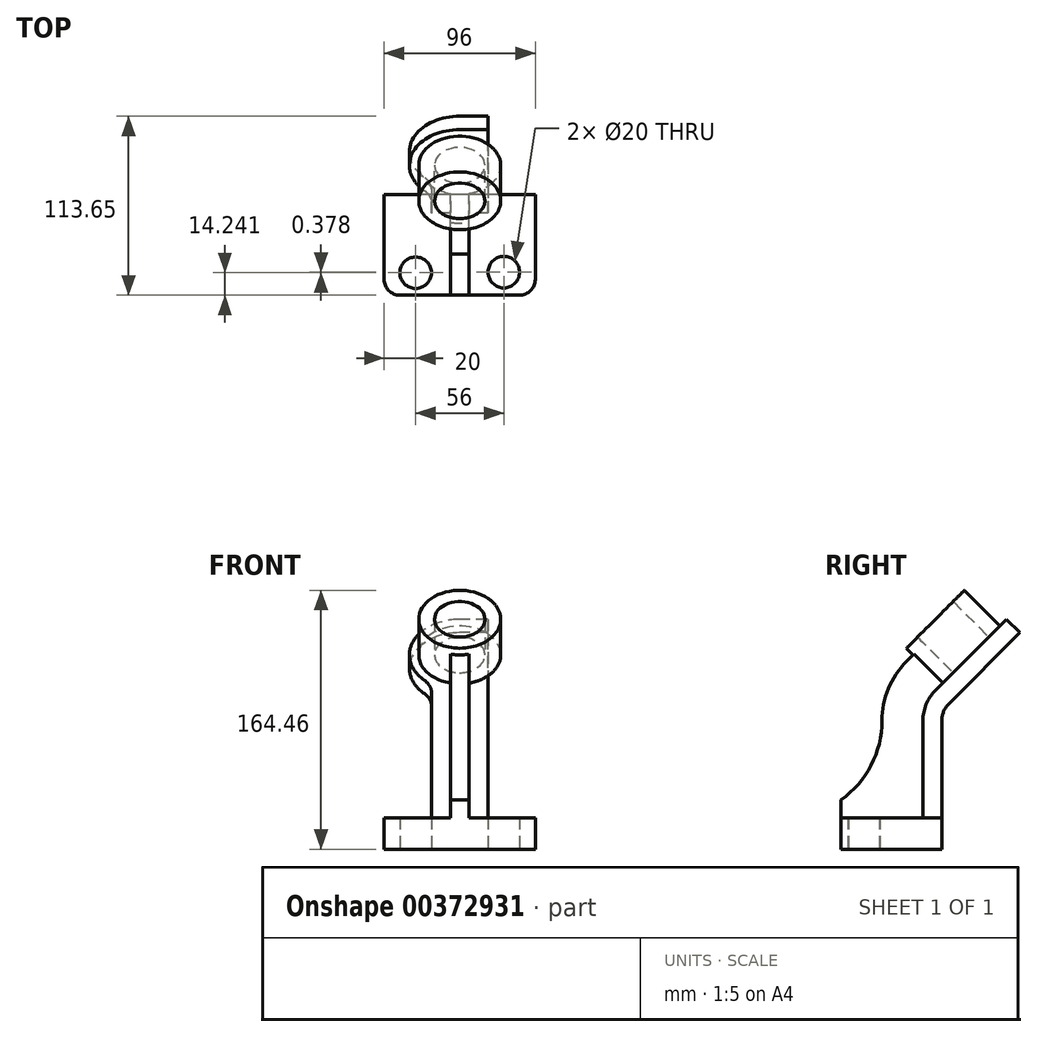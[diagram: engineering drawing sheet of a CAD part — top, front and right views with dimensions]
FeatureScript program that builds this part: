
annotation { "Feature Type Name" : "Feature", "Feature Type Description" : "" }
export const myFeature = defineFeature(function(context is Context, id is Id, definition is map)
    precondition{}
    {
        {
            var Q0;
            Q0=qCreatedBy(makeId("Top.planeOp"),FACE);
            var sketch = newSketch(context, id + "F0", { "sketchPlane" : qUnion([Q0])});
            skLineSegment(sketch, "E0.bottom", {"start": v(48, -32) * mm, "end": v(-48, -32) * mm});
            skLineSegment(sketch, "E0.top", {"start": v(48, 32) * mm, "end": v(-48, 32) * mm});
            skLineSegment(sketch, "E0.left", {"start": v(48, -32) * mm, "end": v(48, 32) * mm});
            skLineSegment(sketch, "E0.right", {"start": v(-48, -32) * mm, "end": v(-48, 32) * mm});
            skPoint(sketch, "E0.middle", {"position": v(0, 0) * mm});
            skCircle(sketch, "E1", {"center": v(28, -17.38) * mm, "radius": 10 * mm});
            skCircle(sketch, "E2", {"center": v(-28, -17.76) * mm, "radius": 10 * mm});
            skSolve(sketch);
        }
        {
            var Q0;
            Q0=makeQuery(id+"F0.imprint","IMPRINT",FACE,{"disambiguationData":[TD([[makeQuery(id+"F0.imprint","IMPRINT",EDGE,{"derivedFrom":sQuery(id+"F0.wireOp",EDGE,"E0.bottom")}),-1.0]])]});
            extrude(context, id + "F1", {"entities" : qUnion([Q0]), "depth" : 20 * mm});
        }
        {
            var Q0;
            Q0=makeQuery(id+"F1.opExtrude","SWEPT_EDGE",EDGE,{"disambiguationData":[OSD([sQuery(id+"F0.wireOp",EDGE,"E0.bottom"),sQuery(id+"F0.wireOp",EDGE,"E0.left")])]});
            var Q1;
            Q1=makeQuery(id+"F1.opExtrude","SWEPT_EDGE",EDGE,{"disambiguationData":[OSD([sQuery(id+"F0.wireOp",EDGE,"E0.bottom"),sQuery(id+"F0.wireOp",EDGE,"E0.right")])]});
            fillet(context, id + "F2", {"entities" : qUnion([Q0, Q1]), "radius" : 10 * mm, "tangentPropagation" : true, "allowEdgeOverflow" : false});
        }
        {
            var Q0;
            Q0=qCreatedBy(makeId("Right.planeOp"),FACE);
            var sketch = newSketch(context, id + "F3", { "sketchPlane" : qUnion([Q0])});
            skLineSegment(sketch, "E3", {"start": v(32, 0) * mm, "end": v(32, 81.73) * mm});
            skLineSegment(sketch, "E4", {"start": v(36.4, 92.34) * mm, "end": v(81.65, 137.6) * mm});
            skPoint(sketch, "E5.visualSharp", {"position": v(32, 87.95) * mm});
            skArc(sketch, "E5.filletArc", {"start": v(36.4, 92.34) * mm, "mid": v(33.14, 87.47) * mm, "end": v(32, 81.73) * mm});
            skLineSegment(sketch, "E6", {"start": v(81.65, 137.6) * mm, "end": v(73.16, 146.08) * mm});
            skLineSegment(sketch, "E7", {"start": v(73.16, 146.08) * mm, "end": v(27.9, 100.82) * mm});
            skLineSegment(sketch, "E8", {"start": v(20, 81.73) * mm, "end": v(20, 0) * mm});
            skLineSegment(sketch, "E9", {"start": v(20, 0) * mm, "end": v(32, 0) * mm});
            skPoint(sketch, "E10.visualSharp", {"position": v(20, 92.92) * mm});
            skArc(sketch, "E10.filletArc", {"start": v(27.9, 100.82) * mm, "mid": v(22.06, 92.06) * mm, "end": v(20, 81.73) * mm});
            skSolve(sketch);
        }
        {
            var Q0;
            Q0=makeQuery(id+"F3.imprint","IMPRINT",FACE,{"disambiguationData":[TD([[makeQuery(id+"F3.imprint","IMPRINT",EDGE,{"derivedFrom":sQuery(id+"F3.wireOp",EDGE,"E3")}),1.0]])]});
            extrude(context, id + "F4", {"entities" : qUnion([Q0]), "operationType" : NewBodyOperationType.ADD, "endBound" : BoundingType.SYMMETRIC, "depth" : 36 * mm});
        }
        {
            var Q0;
            Q0=makeQuery(id+"F4.opExtrude","SWEPT_FACE",FACE,{"disambiguationData":[OSD([sQuery(id+"F3.wireOp",EDGE,"E7")])]});
            var sketch = newSketch(context, id + "F5", { "sketchPlane" : qUnion([Q0])});
            skCircle(sketch, "E11", {"center": v(0, 123.03) * mm, "radius": 32 * mm});
            skSolve(sketch);
        }
        {
            var Q0;
            {var subQ0=sQuery(id+"F5.wireOp",EDGE,"E11");var subQ1=makeQuery(id+"F4.opExtrude","CAP_EDGE",EDGE,{"disambiguationData":[OSD([sQuery(id+"F3.wireOp",EDGE,"E7")])],"isStart":true});var subQ2=makeQuery(id+"F5.imprint","INTERSECT",VERTEX,{"disambiguationData":[OD(0.0)],"derivedFrom":[subQ1,subQ0]});Q0=makeQuery(id+"F5.imprint","IMPRINT",FACE,{"disambiguationData":[TD([[makeQuery(id+"F5.imprint","IMPRINT",EDGE,{"disambiguationData":[TD([[subQ2,-1.0]])],"derivedFrom":subQ0}),1.0]])]});}
            var Q1;
            {var subQ0=sQuery(id+"F5.wireOp",EDGE,"E11");var subQ1=sQuery(id+"F3.wireOp",EDGE,"E7");var subQ6=makeQuery(id+"F4.opExtrude","CAP_EDGE",EDGE,{"disambiguationData":[OSD([subQ1])],"isStart":true});var subQ9=makeQuery(id+"F5.imprint","INTERSECT",VERTEX,{"disambiguationData":[OD(0.0)],"derivedFrom":[subQ6,subQ0]});Q1=makeQuery(id+"F5.imprint","IMPRINT",FACE,{"disambiguationData":[TD([[makeQuery(id+"F5.imprint","IMPRINT",EDGE,{"disambiguationData":[TD([[subQ9,-1.0]])],"derivedFrom":subQ6}),1.0]])]});}
            var Q2;
            {var subQ0=sQuery(id+"F5.wireOp",EDGE,"E11");var subQ1=makeQuery(id+"F4.opExtrude","CAP_EDGE",EDGE,{"disambiguationData":[OSD([sQuery(id+"F3.wireOp",EDGE,"E7")])],"isStart":false});var subQ2=makeQuery(id+"F5.imprint","INTERSECT",VERTEX,{"disambiguationData":[OD(0.0)],"derivedFrom":[subQ1,subQ0]});Q2=makeQuery(id+"F5.imprint","IMPRINT",FACE,{"disambiguationData":[TD([[makeQuery(id+"F5.imprint","IMPRINT",EDGE,{"disambiguationData":[TD([[subQ2,1.0]])],"derivedFrom":subQ0}),1.0]])]});}
            extrude(context, id + "F6", {"entities" : qUnion([Q0, Q1, Q2]), "operationType" : NewBodyOperationType.ADD, "oppositeDirection" : true, "depth" : 12 * mm});
        }
        {
            var Q0;
            {var subQ0=sQuery(id+"F5.wireOp",EDGE,"E11");var subQ1=sQuery(id+"F3.wireOp",EDGE,"E7");var subQ4=makeQuery(id+"F4.opExtrude","CAP_EDGE",EDGE,{"disambiguationData":[OSD([subQ1])],"isStart":true});var subQ5=makeQuery(id+"F5.imprint","INTERSECT",VERTEX,{"disambiguationData":[OD(0.0)],"derivedFrom":[subQ4,subQ0]});Q0=makeQuery(id+"F5.imprint","IMPRINT",FACE,{"disambiguationData":[TD([[makeQuery(id+"F5.imprint","IMPRINT",EDGE,{"disambiguationData":[TD([[subQ5,1.0]])],"derivedFrom":subQ0}),-1.0]])]});}
            var Q1;
            {var subQ0=sQuery(id+"F5.wireOp",EDGE,"E11");var subQ1=sQuery(id+"F3.wireOp",EDGE,"E7");var subQ4=makeQuery(id+"F4.opExtrude","CAP_EDGE",EDGE,{"disambiguationData":[OSD([subQ1])],"isStart":false});var subQ5=makeQuery(id+"F5.imprint","INTERSECT",VERTEX,{"disambiguationData":[OD(0.0)],"derivedFrom":[subQ4,subQ0]});Q1=makeQuery(id+"F5.imprint","IMPRINT",FACE,{"disambiguationData":[TD([[makeQuery(id+"F5.imprint","IMPRINT",EDGE,{"disambiguationData":[TD([[subQ5,-1.0]])],"derivedFrom":subQ0}),-1.0]])]});}
            extrude(context, id + "F7", {"entities" : qUnion([Q0, Q1]), "operationType" : NewBodyOperationType.REMOVE, "oppositeDirection" : true, "depth" : 25 * mm});
        }
        {
            var Q0;
            {var subQ0=sQuery(id+"F5.wireOp",EDGE,"E11");var subQ1=sQuery(id+"F3.wireOp",EDGE,"E7");var subQ6=makeQuery(id+"F4.opExtrude","CAP_EDGE",EDGE,{"disambiguationData":[OSD([subQ1])],"isStart":true});var subQ9=makeQuery(id+"F5.imprint","INTERSECT",VERTEX,{"disambiguationData":[OD(0.0)],"derivedFrom":[subQ6,subQ0]});Q0=makeQuery(id+"F5.imprint","IMPRINT",FACE,{"disambiguationData":[TD([[makeQuery(id+"F5.imprint","IMPRINT",EDGE,{"disambiguationData":[TD([[subQ9,-1.0]])],"derivedFrom":subQ6}),1.0]])]});}
            var sketch = newSketch(context, id + "F8", { "sketchPlane" : qUnion([Q0])});
            skCircle(sketch, "E12", {"center": v(0, 123.03) * mm, "radius": 26 * mm});
            skCircle(sketch, "E13", {"center": v(0, 123.03) * mm, "radius": 16 * mm});
            skSolve(sketch);
        }
        {
            var Q0;
            Q0 = qSketchRegion(id + "F8", true);
            extrude(context, id + "F9", {"entities" : qUnion([Q0]), "operationType" : NewBodyOperationType.ADD, "depth" : 32 * mm});
        }
        {
            var Q0;
            Q0=makeQuery(id+"F6.boolean.opBoolean","INTERSECT",EDGE,{"disambiguationData":[OD(0.0)],"derivedFrom":[makeQuery(id+"F4.opExtrude","CAP_FACE",FACE,{"disambiguationData":[OSD([sQuery(id+"F3.wireOp",EDGE,"E3"),sQuery(id+"F3.wireOp",EDGE,"E4"),sQuery(id+"F3.wireOp",EDGE,"E5.filletArc"),sQuery(id+"F3.wireOp",EDGE,"E6"),sQuery(id+"F3.wireOp",EDGE,"E7"),sQuery(id+"F3.wireOp",EDGE,"E8"),sQuery(id+"F3.wireOp",EDGE,"E9"),sQuery(id+"F3.wireOp",EDGE,"E10.filletArc")])],"isStart":false}),makeQuery(id+"F6.opExtrude","SWEPT_FACE",FACE,{"disambiguationData":[OSD([sQuery(id+"F5.wireOp",EDGE,"E11")])]})]});
            var Q1;
            Q1=makeQuery(id+"F6.boolean.opBoolean","INTERSECT",EDGE,{"disambiguationData":[OD(0.0)],"derivedFrom":[makeQuery(id+"F4.opExtrude","CAP_FACE",FACE,{"disambiguationData":[OSD([sQuery(id+"F3.wireOp",EDGE,"E3"),sQuery(id+"F3.wireOp",EDGE,"E4"),sQuery(id+"F3.wireOp",EDGE,"E5.filletArc"),sQuery(id+"F3.wireOp",EDGE,"E6"),sQuery(id+"F3.wireOp",EDGE,"E7"),sQuery(id+"F3.wireOp",EDGE,"E8"),sQuery(id+"F3.wireOp",EDGE,"E9"),sQuery(id+"F3.wireOp",EDGE,"E10.filletArc")])],"isStart":true}),makeQuery(id+"F6.opExtrude","SWEPT_FACE",FACE,{"disambiguationData":[OSD([sQuery(id+"F5.wireOp",EDGE,"E11")])]})]});
            fillet(context, id + "F10", {"entities" : qUnion([Q0, Q1]), "radius" : 15 * mm, "tangentPropagation" : true, "allowEdgeOverflow" : false});
        }
        {
            var Q0;
            Q0=qCreatedBy(makeId("Right.planeOp"),FACE);
            var sketch = newSketch(context, id + "F11", { "sketchPlane" : qUnion([Q0])});
            skLineSegment(sketch, "E14.0", {"start": v(20, 81.73) * mm, "end": v(20, 0) * mm});
            skArc(sketch, "E15.0", {"start": v(27.9, 100.82) * mm, "mid": v(22.06, 92.06) * mm, "end": v(20, 81.73) * mm});
            skLineSegment(sketch, "E16.0", {"start": v(27.9, 100.82) * mm, "end": v(35.4, 108.31) * mm});
            skLineSegment(sketch, "E17.0", {"start": v(9.52, 119.2) * mm, "end": v(17.01, 126.7) * mm});
            skArc(sketch, "E17.1", {"start": v(9.52, 119.2) * mm, "mid": v(-1.97, 102.01) * mm, "end": v(-6, 81.73) * mm});
            skArc(sketch, "E18", {"start": v(-32, 31.4) * mm, "mid": v(-12.88, 53.4) * mm, "end": v(-6, 81.73) * mm});
            skLineSegment(sketch, "E19.0", {"start": v(-32, 0) * mm, "end": v(-32, 20) * mm});
            skLineSegment(sketch, "E20", {"start": v(-32, 20) * mm, "end": v(-32, 31.4) * mm});
            skLineSegment(sketch, "E21", {"start": v(17.01, 126.7) * mm, "end": v(35.4, 108.31) * mm});
            skPoint(sketch, "E22.orphan", {"position": v(73.16, 146.08) * mm});
            skLineSegment(sketch, "E23", {"start": v(-32, 0) * mm, "end": v(20, 0) * mm});
            skSolve(sketch);
        }
        {
            var Q0;
            Q0=makeQuery(id+"F11.imprint","IMPRINT",FACE,{"disambiguationData":[TD([[makeQuery(id+"F11.imprint","IMPRINT",EDGE,{"derivedFrom":sQuery(id+"F11.wireOp",EDGE,"E14.0")}),-1.0]])]});
            extrude(context, id + "F12", {"entities" : qUnion([Q0]), "operationType" : NewBodyOperationType.ADD, "endBound" : BoundingType.SYMMETRIC, "depth" : 12 * mm});
        }
    });
